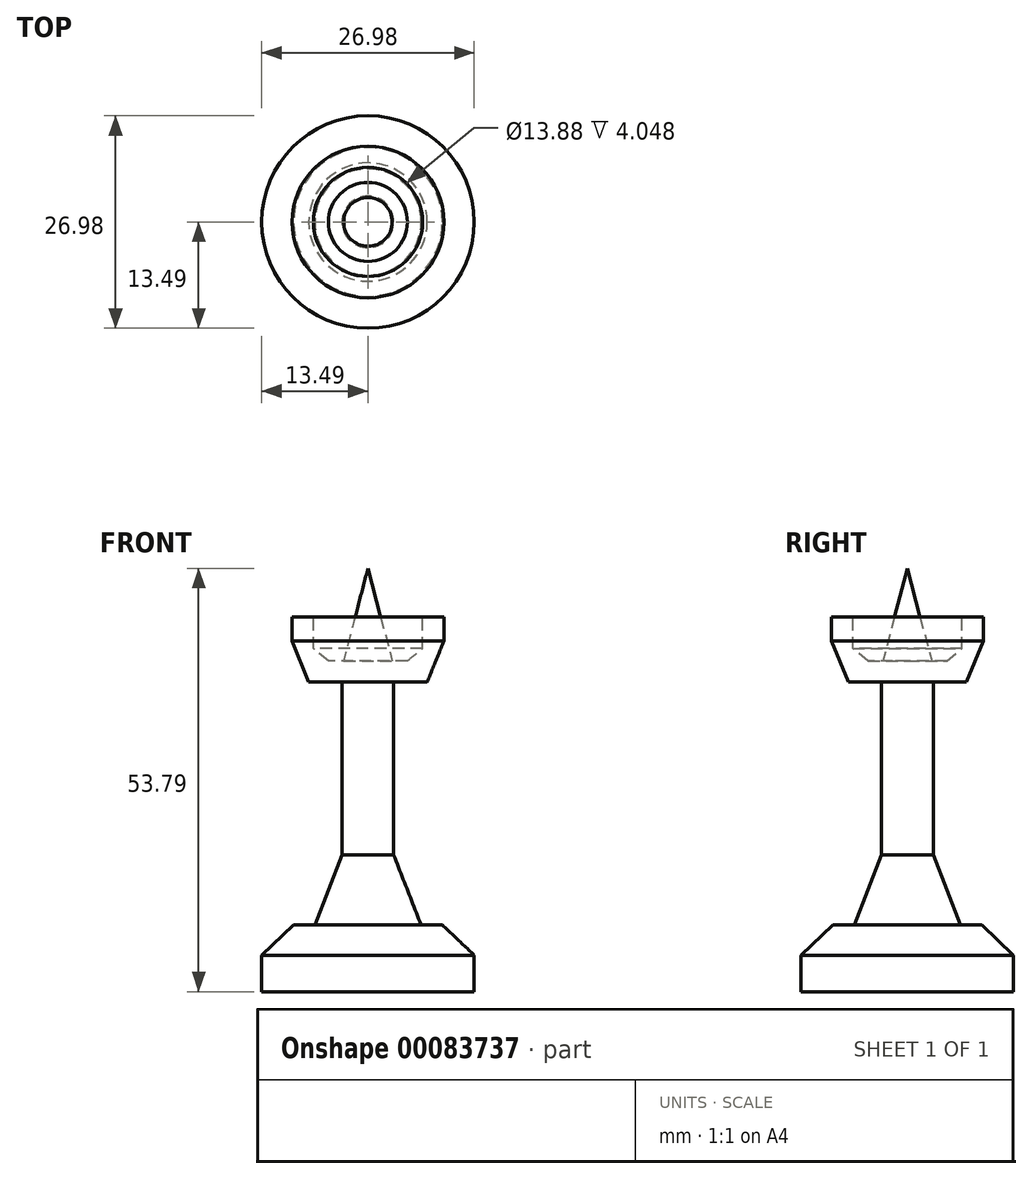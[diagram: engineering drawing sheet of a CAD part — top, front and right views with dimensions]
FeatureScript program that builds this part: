
annotation { "Feature Type Name" : "Feature", "Feature Type Description" : "" }
export const myFeature = defineFeature(function(context is Context, id is Id, definition is map)
    precondition{}
    {
        {
            var Q0;
            Q0=qCreatedBy(makeId("Front.planeOp"),FACE);
            var sketch = newSketch(context, id + "F0", { "sketchPlane" : qUnion([Q0])});
            skLineSegment(sketch, "E0", {"start": v(0, -27.09) * mm, "end": v(-13.5, -27.09) * mm});
            skLineSegment(sketch, "E1", {"start": v(-13.5, -27.09) * mm, "end": v(-13.5, -22.46) * mm});
            skLineSegment(sketch, "E2", {"start": v(-13.5, -22.46) * mm, "end": v(-9.45, -18.6) * mm});
            skLineSegment(sketch, "E3", {"start": v(-9.45, -18.6) * mm, "end": v(-6.75, -18.6) * mm});
            skLineSegment(sketch, "E4", {"start": v(-6.75, -18.6) * mm, "end": v(-3.28, -9.74) * mm});
            skLineSegment(sketch, "E5", {"start": v(-3.28, -9.74) * mm, "end": v(-3.28, 12.24) * mm});
            skLineSegment(sketch, "E6", {"start": v(-3.28, 12.24) * mm, "end": v(-7.52, 12.24) * mm});
            skLineSegment(sketch, "E7", {"start": v(-7.52, 12.24) * mm, "end": v(-9.64, 17.45) * mm});
            skLineSegment(sketch, "E8", {"start": v(-9.64, 17.45) * mm, "end": v(-9.64, 20.53) * mm});
            skLineSegment(sketch, "E9", {"start": v(-9.64, 20.53) * mm, "end": v(-6.94, 20.53) * mm});
            skLineSegment(sketch, "E10", {"start": v(-6.94, 20.53) * mm, "end": v(-6.94, 16.48) * mm});
            skLineSegment(sketch, "E11", {"start": v(-6.94, 16.48) * mm, "end": v(-5.01, 14.94) * mm});
            skLineSegment(sketch, "E12", {"start": v(-5.01, 14.94) * mm, "end": v(-3.08, 14.94) * mm});
            skLineSegment(sketch, "E13", {"start": v(-3.08, 14.94) * mm, "end": v(0, 26.7) * mm});
            skLineSegment(sketch, "E14", {"start": v(0, 26.7) * mm, "end": v(0, -27.09) * mm});
            skSolve(sketch);
        }
        {
            var Q0;
            Q0 = qSketchRegion(id + "F0", true);
            var Q1;
            Q1=sQuery(id+"F0.wireOp",EDGE,"E14");
            revolve(context, id + "F1", {"entities" : qUnion([Q0]), "axis" : qUnion([Q1]), "revolveType" : RevolveType.FULL});
        }
    });
